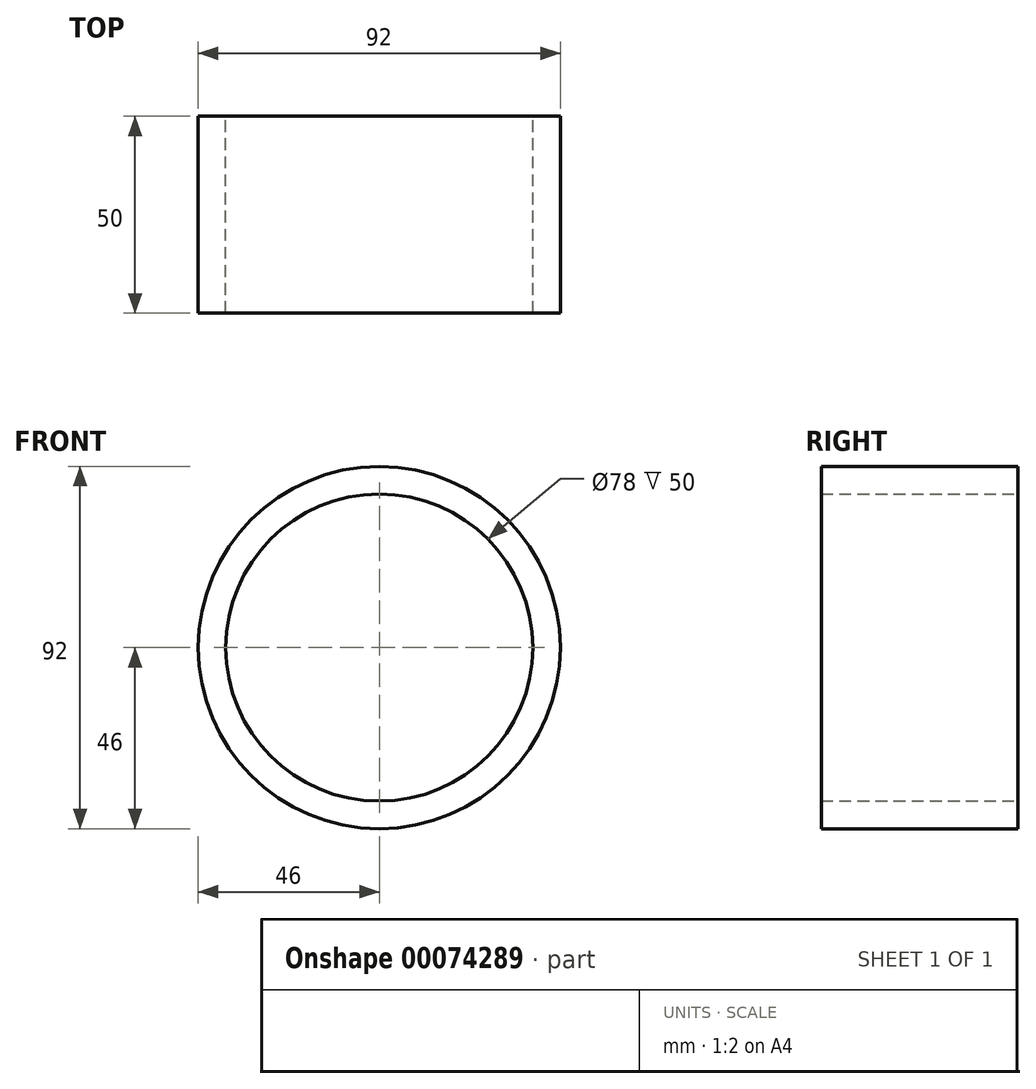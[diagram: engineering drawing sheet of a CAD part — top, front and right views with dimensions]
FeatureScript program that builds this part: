
annotation { "Feature Type Name" : "Feature", "Feature Type Description" : "" }
export const myFeature = defineFeature(function(context is Context, id is Id, definition is map)
    precondition{}
    {
        {
            var Q0;
            Q0=qCreatedBy(makeId("Front.planeOp"),FACE);
            var sketch = newSketch(context, id + "F0", { "sketchPlane" : qUnion([Q0])});
            skCircle(sketch, "E0", {"center": v(0, 0) * mm, "radius": 46 * mm});
            skCircle(sketch, "E1", {"center": v(0, 0) * mm, "radius": 39 * mm});
            skSolve(sketch);
        }
        {
            var Q0;
            Q0 = qSketchRegion(id + "F0", true);
            extrude(context, id + "F1", {"entities" : qUnion([Q0]), "depth" : 50 * mm});
        }
    });
